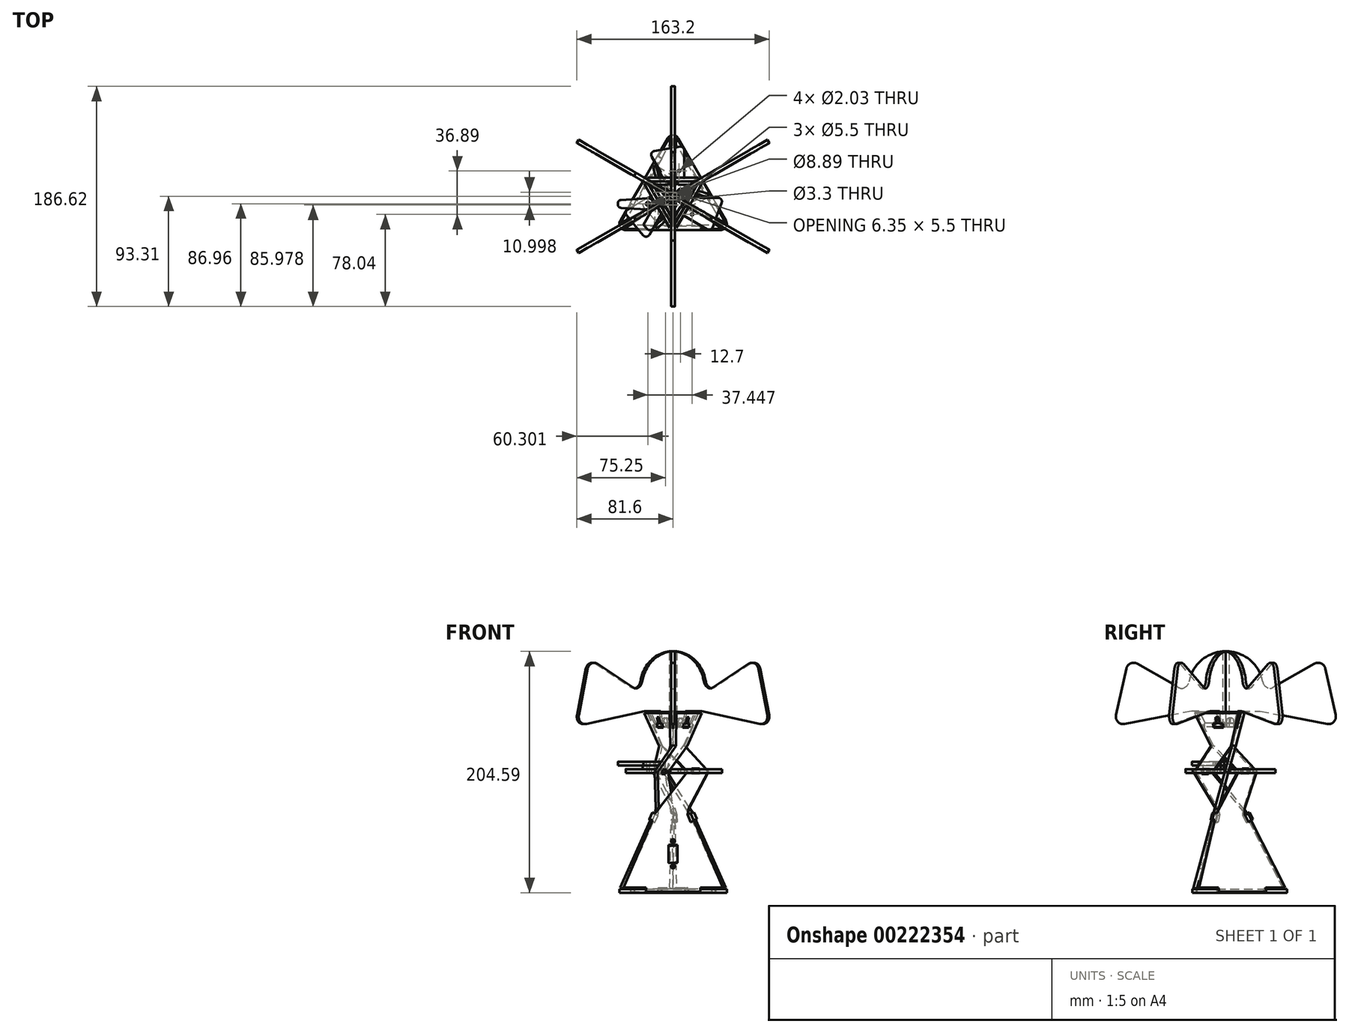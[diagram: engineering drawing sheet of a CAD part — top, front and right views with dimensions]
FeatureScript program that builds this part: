
annotation { "Feature Type Name" : "Feature", "Feature Type Description" : "" }
export const myFeature = defineFeature(function(context is Context, id is Id, definition is map)
    precondition{}
    {
        {
            var Q0;
            Q0=qCreatedBy(makeId("Front.planeOp"),FACE);
            var sketch = newSketch(context, id + "F0", { "sketchPlane" : qUnion([Q0])});
            skLineSegment(sketch, "E0", {"start": v(0, 0) * mm, "end": v(0, 152.4) * mm});
            skSolve(sketch);
        }
        {
            var Q0;
            Q0=qCreatedBy(makeId("Right.planeOp"),FACE);
            var sketch = newSketch(context, id + "F1", { "sketchPlane" : qUnion([Q0])});
            skLineSegment(sketch, "E1", {"start": v(0, 0) * mm, "end": v(-25.4, 0) * mm});
            skLineSegment(sketch, "E2", {"start": v(-25.4, 0) * mm, "end": v(15.88, 152.4) * mm});
            skLineSegment(sketch, "E3", {"start": v(15.88, 152.4) * mm, "end": v(0, 152.4) * mm});
            skLineSegment(sketch, "E4", {"start": v(0, 152.4) * mm, "end": v(0, 0) * mm});
            skPoint(sketch, "E5", {"position": v(0, 93.78) * mm});
            skSolve(sketch);
        }
        {
            var Q0;
            Q0=sQuery(id+"F1.wireOp",EDGE,"E2");
            var Q1;
            Q1=qCreatedBy(makeId("Front.planeOp"),FACE);
            cPlane(context, id + "F2", {"entities" : qUnion([Q0, Q1]), "cplaneType" : CPlaneType.LINE_ANGLE, "offset" : 25.4 * mm, "angle" : 0 * degree, "width" : 152.4 * mm, "height" : 152.4 * mm});
        }
        {
            var Q0;
            Q0=qCreatedBy(id+"F2.planeOp",FACE);
            var sketch = newSketch(context, id + "F3", { "sketchPlane" : qUnion([Q0])});
            skLineSegment(sketch, "E6", {"start": v(-43.56, -6.64) * mm, "end": v(43.56, -6.64) * mm});
            skLineSegment(sketch, "E7", {"start": v(43.56, -6.64) * mm, "end": v(15.2, 62.08) * mm});
            skLineSegment(sketch, "E8", {"start": v(15.2, 62.08) * mm, "end": v(-12.3, 99.06) * mm});
            skLineSegment(sketch, "E9", {"start": v(-12.3, 99.06) * mm, "end": v(9.57, 122.12) * mm});
            skLineSegment(sketch, "E10", {"start": v(9.57, 122.12) * mm, "end": v(21.59, 151.25) * mm});
            skLineSegment(sketch, "E11", {"start": v(21.59, 151.25) * mm, "end": v(-21.6, 151.25) * mm});
            skLineSegment(sketch, "E12", {"start": v(-21.6, 151.25) * mm, "end": v(-9.57, 122.12) * mm});
            skLineSegment(sketch, "E13", {"start": v(-9.57, 122.12) * mm, "end": v(-29.83, 99.06) * mm});
            skLineSegment(sketch, "E14", {"start": v(-29.83, 99.06) * mm, "end": v(-13.3, 66.7) * mm});
            skLineSegment(sketch, "E15", {"start": v(-13.3, 66.7) * mm, "end": v(-43.56, -6.64) * mm});
            skLineSegment(sketch, "E16", {"start": v(-42.1, -3.08) * mm, "end": v(-23.04, -3.08) * mm});
            skLineSegment(sketch, "E17", {"start": v(-23.04, -3.08) * mm, "end": v(-23.04, -6.64) * mm});
            skLineSegment(sketch, "E18", {"start": v(23.04, -6.64) * mm, "end": v(23.04, -3.08) * mm});
            skLineSegment(sketch, "E19", {"start": v(23.04, -3.08) * mm, "end": v(42.1, -3.08) * mm});
            skSolve(sketch);
        }
        {
            var Q0;
            {var subQ6=sQuery(id+"F3.wireOp",EDGE,"E8");Q0=makeQuery(id+"F3.imprint","IMPRINT",FACE,{"disambiguationData":[TD([[makeQuery(id+"F3.imprint","IMPRINT",EDGE,{"derivedFrom":subQ6}),1.0]])]});}
            extrude(context, id + "F4", {"entities" : qUnion([Q0]), "oppositeDirection" : true, "depth" : 3.17 * mm});
        }
        {
            var Q0;
            Q0=makeQuery(id+"F4.opExtrude","CAP_FACE",FACE,{"disambiguationData":[OSD([sQuery(id+"F3.wireOp",EDGE,"E6"),sQuery(id+"F3.wireOp",EDGE,"E7"),sQuery(id+"F3.wireOp",EDGE,"E8"),sQuery(id+"F3.wireOp",EDGE,"E9"),sQuery(id+"F3.wireOp",EDGE,"E10"),sQuery(id+"F3.wireOp",EDGE,"E11"),sQuery(id+"F3.wireOp",EDGE,"E12"),sQuery(id+"F3.wireOp",EDGE,"E13"),sQuery(id+"F3.wireOp",EDGE,"E14"),sQuery(id+"F3.wireOp",EDGE,"E15")])],"isStart":false});
            var sketch = newSketch(context, id + "F5", { "sketchPlane" : qUnion([Q0])});
            skLineSegment(sketch, "E20", {"start": v(-15.2, 62.08) * mm, "end": v(-17.55, 63.05) * mm});
            skLineSegment(sketch, "E21", {"start": v(-17.55, 63.05) * mm, "end": v(-19.97, 57.18) * mm});
            skLineSegment(sketch, "E22", {"start": v(-19.97, 57.18) * mm, "end": v(-17.63, 56.21) * mm});
            skLineSegment(sketch, "E23", {"start": v(-17.63, 56.21) * mm, "end": v(-15.2, 62.08) * mm});
            skSolve(sketch);
        }
        {
            var Q0;
            Q0 = qSketchRegion(id + "F5", true);
            extrude(context, id + "F6", {"entities" : qUnion([Q0]), "operationType" : NewBodyOperationType.ADD, "oppositeDirection" : true, "depth" : 3.17 * mm});
        }
        {
            var Q0;
            Q0=makeQuery(id+"F6.boolean.opBoolean","MERGE",FACE,{"derivedFrom":[makeQuery(id+"F4.opExtrude","CAP_FACE",FACE,{"disambiguationData":[OSD([sQuery(id+"F3.wireOp",EDGE,"E6"),sQuery(id+"F3.wireOp",EDGE,"E7"),sQuery(id+"F3.wireOp",EDGE,"E8"),sQuery(id+"F3.wireOp",EDGE,"E9"),sQuery(id+"F3.wireOp",EDGE,"E10"),sQuery(id+"F3.wireOp",EDGE,"E11"),sQuery(id+"F3.wireOp",EDGE,"E12"),sQuery(id+"F3.wireOp",EDGE,"E13"),sQuery(id+"F3.wireOp",EDGE,"E14"),sQuery(id+"F3.wireOp",EDGE,"E15")])],"isStart":false}),makeQuery(id+"F6.opExtrude","CAP_FACE",FACE,{"disambiguationData":[OSD([sQuery(id+"F5.wireOp",EDGE,"E20"),sQuery(id+"F5.wireOp",EDGE,"E21"),sQuery(id+"F5.wireOp",EDGE,"E22"),sQuery(id+"F5.wireOp",EDGE,"E23")])],"isStart":true})]});
            var sketch = newSketch(context, id + "F7", { "sketchPlane" : qUnion([Q0])});
            skLineSegment(sketch, "E24", {"start": v(12.2, 61.04) * mm, "end": v(14.82, 54.7) * mm});
            skLineSegment(sketch, "E25", {"start": v(12.2, 61.04) * mm, "end": v(15.14, 62.25) * mm});
            skLineSegment(sketch, "E26", {"start": v(17.75, 55.9) * mm, "end": v(15.14, 62.25) * mm});
            skLineSegment(sketch, "E27", {"start": v(17.75, 55.9) * mm, "end": v(14.82, 54.7) * mm});
            skLineSegment(sketch, "E28", {"start": v(13.3, 66.7) * mm, "end": v(12.2, 61.04) * mm});
            skLineSegment(sketch, "E29", {"start": v(15.14, 62.25) * mm, "end": v(13.3, 66.7) * mm});
            skSolve(sketch);
        }
        {
            var Q0;
            Q0 = qSketchRegion(id + "F7", true);
            extrude(context, id + "F8", {"entities" : qUnion([Q0]), "operationType" : NewBodyOperationType.REMOVE, "oppositeDirection" : true, "depth" : 25.4 * mm});
        }
        {
            var Q0;
            Q0=qCreatedBy(id+"F2.planeOp",FACE);
            var sketch = newSketch(context, id + "F9", { "sketchPlane" : qUnion([Q0])});
            skLineSegment(sketch, "E30.bottom", {"start": v(4.76, 142.08) * mm, "end": v(-4.76, 142.08) * mm});
            skLineSegment(sketch, "E30.top", {"start": v(4.76, 138.14) * mm, "end": v(-4.76, 138.14) * mm});
            skLineSegment(sketch, "E30.left", {"start": v(4.76, 142.08) * mm, "end": v(4.76, 138.14) * mm});
            skLineSegment(sketch, "E30.right", {"start": v(-4.76, 142.08) * mm, "end": v(-4.76, 138.14) * mm});
            skPoint(sketch, "E31", {"position": v(0, 138.14) * mm});
            skLineSegment(sketch, "E32.top", {"start": v(-1.59, 147.41) * mm, "end": v(1.59, 147.41) * mm});
            skLineSegment(sketch, "E32.left", {"start": v(-1.59, 142.08) * mm, "end": v(-1.59, 147.41) * mm});
            skLineSegment(sketch, "E32.right", {"start": v(1.59, 142.08) * mm, "end": v(1.59, 147.41) * mm});
            skLineSegment(sketch, "E33", {"start": v(0, 147.41) * mm, "end": v(0, 138.14) * mm, "construction": true});
            skSolve(sketch);
        }
        {
            var Q0;
            Q0 = qSketchRegion(id + "F9", true);
            extrude(context, id + "F10", {"entities" : qUnion([Q0]), "operationType" : NewBodyOperationType.REMOVE, "oppositeDirection" : true, "depth" : 25.4 * mm});
        }
        {
            var Q0;
            Q0=makeQuery(id+"F6.boolean.opBoolean","MERGE",FACE,{"derivedFrom":[makeQuery(id+"F4.opExtrude","CAP_FACE",FACE,{"disambiguationData":[OSD([sQuery(id+"F3.wireOp",EDGE,"E6"),sQuery(id+"F3.wireOp",EDGE,"E7"),sQuery(id+"F3.wireOp",EDGE,"E8"),sQuery(id+"F3.wireOp",EDGE,"E9"),sQuery(id+"F3.wireOp",EDGE,"E10"),sQuery(id+"F3.wireOp",EDGE,"E11"),sQuery(id+"F3.wireOp",EDGE,"E12"),sQuery(id+"F3.wireOp",EDGE,"E13"),sQuery(id+"F3.wireOp",EDGE,"E14"),sQuery(id+"F3.wireOp",EDGE,"E15"),sQuery(id+"F3.wireOp",EDGE,"E16"),sQuery(id+"F3.wireOp",EDGE,"E17"),sQuery(id+"F3.wireOp",EDGE,"E18"),sQuery(id+"F3.wireOp",EDGE,"E19")])],"isStart":false}),makeQuery(id+"F6.opExtrude","CAP_FACE",FACE,{"disambiguationData":[OSD([sQuery(id+"F5.wireOp",EDGE,"E20"),sQuery(id+"F5.wireOp",EDGE,"E21"),sQuery(id+"F5.wireOp",EDGE,"E22"),sQuery(id+"F5.wireOp",EDGE,"E23")])],"isStart":true})]});
            var sketch = newSketch(context, id + "F11", { "sketchPlane" : qUnion([Q0])});
            skLineSegment(sketch, "E34.bottom", {"start": v(15.88, 97.66) * mm, "end": v(22.48, 97.66) * mm});
            skLineSegment(sketch, "E34.top", {"start": v(15.88, 101.6) * mm, "end": v(22.48, 101.6) * mm});
            skLineSegment(sketch, "E34.left", {"start": v(15.88, 101.6) * mm, "end": v(15.88, 97.66) * mm});
            skLineSegment(sketch, "E34.right", {"start": v(22.48, 101.6) * mm, "end": v(22.48, 97.66) * mm});
            skSolve(sketch);
        }
        {
            var Q0;
            Q0 = qSketchRegion(id + "F11", true);
            extrude(context, id + "F12", {"entities" : qUnion([Q0]), "operationType" : NewBodyOperationType.REMOVE, "oppositeDirection" : true, "depth" : 25.4 * mm});
        }
        {
            var Q0;
            Q0=makeQuery(id+"F4.opExtrude","SWEPT_BODY",BODY,{"disambiguationData":[OSD([sQuery(id+"F3.wireOp",EDGE,"E6"),sQuery(id+"F3.wireOp",EDGE,"E7"),sQuery(id+"F3.wireOp",EDGE,"E8"),sQuery(id+"F3.wireOp",EDGE,"E9"),sQuery(id+"F3.wireOp",EDGE,"E10"),sQuery(id+"F3.wireOp",EDGE,"E11"),sQuery(id+"F3.wireOp",EDGE,"E12"),sQuery(id+"F3.wireOp",EDGE,"E13"),sQuery(id+"F3.wireOp",EDGE,"E14"),sQuery(id+"F3.wireOp",EDGE,"E15")])]});
            var Q1;
            Q1=sQuery(id+"F1.wireOp",EDGE,"E4");
            circularPattern(context, id + "F13", {"entities" : qUnion([Q0]), "axis" : qUnion([Q1]), "angle" : 360 * degree, "instanceCount" : 3, "equalSpace" : true});
        }
        {
            var Q0;
            Q0=makeQuery(id+"F10.boolean.opBoolean","INTERSECT",VERTEX,{"derivedFrom":[makeQuery(id+"F6.boolean.opBoolean","MERGE",FACE,{"derivedFrom":[makeQuery(id+"F4.opExtrude","CAP_FACE",FACE,{"disambiguationData":[OSD([sQuery(id+"F3.wireOp",EDGE,"E6"),sQuery(id+"F3.wireOp",EDGE,"E7"),sQuery(id+"F3.wireOp",EDGE,"E8"),sQuery(id+"F3.wireOp",EDGE,"E9"),sQuery(id+"F3.wireOp",EDGE,"E10"),sQuery(id+"F3.wireOp",EDGE,"E11"),sQuery(id+"F3.wireOp",EDGE,"E12"),sQuery(id+"F3.wireOp",EDGE,"E13"),sQuery(id+"F3.wireOp",EDGE,"E14"),sQuery(id+"F3.wireOp",EDGE,"E15")])],"isStart":false}),makeQuery(id+"F6.opExtrude","CAP_FACE",FACE,{"disambiguationData":[OSD([sQuery(id+"F5.wireOp",EDGE,"E20"),sQuery(id+"F5.wireOp",EDGE,"E21"),sQuery(id+"F5.wireOp",EDGE,"E22"),sQuery(id+"F5.wireOp",EDGE,"E23")])],"isStart":true})]}),makeQuery(id+"F10.opExtrude","SWEPT_FACE",FACE,{"disambiguationData":[OSD([sQuery(id+"F9.wireOp",EDGE,"E30.top")])]}),makeQuery(id+"F10.opExtrude","SWEPT_FACE",FACE,{"disambiguationData":[OSD([sQuery(id+"F9.wireOp",EDGE,"E30.right")])]})]});
            var Q1;
            Q1=makeQuery(id+"F13.opPattern","COPY",VERTEX,{"derivedFrom":makeQuery(id+"F10.boolean.opBoolean","INTERSECT",VERTEX,{"derivedFrom":[makeQuery(id+"F6.boolean.opBoolean","MERGE",FACE,{"derivedFrom":[makeQuery(id+"F4.opExtrude","CAP_FACE",FACE,{"disambiguationData":[OSD([sQuery(id+"F3.wireOp",EDGE,"E6"),sQuery(id+"F3.wireOp",EDGE,"E7"),sQuery(id+"F3.wireOp",EDGE,"E8"),sQuery(id+"F3.wireOp",EDGE,"E9"),sQuery(id+"F3.wireOp",EDGE,"E10"),sQuery(id+"F3.wireOp",EDGE,"E11"),sQuery(id+"F3.wireOp",EDGE,"E12"),sQuery(id+"F3.wireOp",EDGE,"E13"),sQuery(id+"F3.wireOp",EDGE,"E14"),sQuery(id+"F3.wireOp",EDGE,"E15")])],"isStart":false}),makeQuery(id+"F6.opExtrude","CAP_FACE",FACE,{"disambiguationData":[OSD([sQuery(id+"F5.wireOp",EDGE,"E20"),sQuery(id+"F5.wireOp",EDGE,"E21"),sQuery(id+"F5.wireOp",EDGE,"E22"),sQuery(id+"F5.wireOp",EDGE,"E23")])],"isStart":true})]}),makeQuery(id+"F10.opExtrude","SWEPT_FACE",FACE,{"disambiguationData":[OSD([sQuery(id+"F9.wireOp",EDGE,"E30.top")])]}),makeQuery(id+"F10.opExtrude","SWEPT_FACE",FACE,{"disambiguationData":[OSD([sQuery(id+"F9.wireOp",EDGE,"E30.right")])]})]}),"instanceName":"1"});
            var Q2;
            Q2=makeQuery(id+"F13.opPattern","COPY",VERTEX,{"derivedFrom":makeQuery(id+"F10.boolean.opBoolean","INTERSECT",VERTEX,{"derivedFrom":[makeQuery(id+"F6.boolean.opBoolean","MERGE",FACE,{"derivedFrom":[makeQuery(id+"F4.opExtrude","CAP_FACE",FACE,{"disambiguationData":[OSD([sQuery(id+"F3.wireOp",EDGE,"E6"),sQuery(id+"F3.wireOp",EDGE,"E7"),sQuery(id+"F3.wireOp",EDGE,"E8"),sQuery(id+"F3.wireOp",EDGE,"E9"),sQuery(id+"F3.wireOp",EDGE,"E10"),sQuery(id+"F3.wireOp",EDGE,"E11"),sQuery(id+"F3.wireOp",EDGE,"E12"),sQuery(id+"F3.wireOp",EDGE,"E13"),sQuery(id+"F3.wireOp",EDGE,"E14"),sQuery(id+"F3.wireOp",EDGE,"E15")])],"isStart":false}),makeQuery(id+"F6.opExtrude","CAP_FACE",FACE,{"disambiguationData":[OSD([sQuery(id+"F5.wireOp",EDGE,"E20"),sQuery(id+"F5.wireOp",EDGE,"E21"),sQuery(id+"F5.wireOp",EDGE,"E22"),sQuery(id+"F5.wireOp",EDGE,"E23")])],"isStart":true})]}),makeQuery(id+"F10.opExtrude","SWEPT_FACE",FACE,{"disambiguationData":[OSD([sQuery(id+"F9.wireOp",EDGE,"E30.top")])]}),makeQuery(id+"F10.opExtrude","SWEPT_FACE",FACE,{"disambiguationData":[OSD([sQuery(id+"F9.wireOp",EDGE,"E30.right")])]})]}),"instanceName":"2"});
            cPlane(context, id + "F14", {"entities" : qUnion([Q0, Q1, Q2]), "cplaneType" : CPlaneType.THREE_POINT, "offset" : 25.4 * mm, "width" : 152.4 * mm, "height" : 152.4 * mm});
        }
        {
            var Q0;
            Q0=qCreatedBy(id+"F14.planeOp",FACE);
            var sketch = newSketch(context, id + "F15", { "sketchPlane" : qUnion([Q0])});
            skLineSegment(sketch, "E35", {"start": v(-16.98, 9.8) * mm, "end": v(-10.71, -1.05) * mm});
            skLineSegment(sketch, "E36", {"start": v(-10.71, -1.05) * mm, "end": v(-13.35, -2.58) * mm});
            skLineSegment(sketch, "E37", {"start": v(-13.35, -2.58) * mm, "end": v(-8.9, -10.28) * mm});
            skLineSegment(sketch, "E38", {"start": v(-8.9, -10.28) * mm, "end": v(-6.27, -8.75) * mm});
            skLineSegment(sketch, "E39", {"start": v(-6.27, -8.75) * mm, "end": v(0, -19.6) * mm});
            skLineSegment(sketch, "E40", {"start": v(-11.13, -6.43) * mm, "end": v(-8.13, -4.7) * mm, "construction": true});
            skLineSegment(sketch, "E41.1.0", {"start": v(0, -19.6) * mm, "end": v(6.27, -8.75) * mm});
            skLineSegment(sketch, "E41.1.1", {"start": v(6.27, -8.75) * mm, "end": v(8.9, -10.28) * mm});
            skLineSegment(sketch, "E41.1.2", {"start": v(8.9, -10.28) * mm, "end": v(13.35, -2.58) * mm});
            skLineSegment(sketch, "E41.1.3", {"start": v(10.71, -1.05) * mm, "end": v(16.98, 9.8) * mm});
            skLineSegment(sketch, "E41.1.4", {"start": v(13.35, -2.58) * mm, "end": v(10.71, -1.05) * mm});
            skLineSegment(sketch, "E41.2.0", {"start": v(16.98, 9.8) * mm, "end": v(4.44, 9.8) * mm});
            skLineSegment(sketch, "E41.2.1", {"start": v(4.44, 9.8) * mm, "end": v(4.44, 12.85) * mm});
            skLineSegment(sketch, "E41.2.2", {"start": v(4.44, 12.85) * mm, "end": v(-4.45, 12.85) * mm});
            skLineSegment(sketch, "E41.2.3", {"start": v(-4.45, 9.8) * mm, "end": v(-16.98, 9.8) * mm});
            skLineSegment(sketch, "E41.2.4", {"start": v(-4.45, 12.85) * mm, "end": v(-4.45, 9.8) * mm});
            skPoint(sketch, "E41.center", {"position": v(0, 0) * mm});
            skCircle(sketch, "E42", {"center": v(6.35, 3.67) * mm, "radius": 2.75 * mm});
            skCircle(sketch, "E43", {"center": v(0, -7.33) * mm, "radius": 2.75 * mm});
            skCircle(sketch, "E44", {"center": v(-6.35, 3.67) * mm, "radius": 2.75 * mm});
            skLineSegment(sketch, "E45", {"start": v(-6.35, 3.67) * mm, "end": v(6.35, 3.67) * mm, "construction": true});
            skLineSegment(sketch, "E46", {"start": v(6.35, 3.67) * mm, "end": v(0, -7.33) * mm, "construction": true});
            skLineSegment(sketch, "E47", {"start": v(-6.35, 3.67) * mm, "end": v(0, -7.33) * mm, "construction": true});
            skLineSegment(sketch, "E48", {"start": v(0, -7.33) * mm, "end": v(0, 3.67) * mm, "construction": true});
            skLineSegment(sketch, "E49", {"start": v(-6.35, 3.67) * mm, "end": v(3.17, -1.83) * mm, "construction": true});
            skSolve(sketch);
        }
        {
            var Q0;
            Q0 = qSketchRegion(id + "F15", true);
            extrude(context, id + "F16", {"entities" : qUnion([Q0]), "depth" : 3.17 * mm});
        }
        {
            var Q0;
            Q0=qCreatedBy(makeId("Right.planeOp"),FACE);
            var sketch = newSketch(context, id + "F17", { "sketchPlane" : qUnion([Q0])});
            skLineSegment(sketch, "E50", {"start": v(-17.46, 143.75) * mm, "end": v(-22.6, 153.91) * mm});
            skLineSegment(sketch, "E51", {"start": v(-17.46, 143.75) * mm, "end": v(10.24, 143.75) * mm, "construction": true});
            skLineSegment(sketch, "E52", {"start": v(10.24, 143.75) * mm, "end": v(13, 153.91) * mm});
            skLineSegment(sketch, "E53", {"start": v(13, 153.91) * mm, "end": v(28.95, 153.91) * mm});
            skLineSegment(sketch, "E54", {"start": v(-22.6, 153.91) * mm, "end": v(-28.95, 153.91) * mm});
            skLineSegment(sketch, "E55", {"start": v(-4.58, 143.75) * mm, "end": v(-4.58, 145.34) * mm});
            skLineSegment(sketch, "E56", {"start": v(-4.58, 145.34) * mm, "end": v(-10.08, 145.34) * mm, "construction": true});
            skLineSegment(sketch, "E57", {"start": v(-10.08, 145.34) * mm, "end": v(-10.08, 143.75) * mm});
            skArc(sketch, "E58", {"start": v(-4.58, 145.34) * mm, "mid": v(-7.33, 148.09) * mm, "end": v(-10.08, 145.34) * mm});
            skLineSegment(sketch, "E59", {"start": v(10.24, 143.75) * mm, "end": v(-4.58, 143.75) * mm});
            skLineSegment(sketch, "E60", {"start": v(-10.08, 143.75) * mm, "end": v(-17.46, 143.75) * mm});
            skLineSegment(sketch, "E61", {"start": v(28.95, 153.91) * mm, "end": v(95.25, 141.21) * mm});
            skLineSegment(sketch, "E62", {"start": v(95.25, 141.21) * mm, "end": v(82.55, 198.36) * mm});
            skLineSegment(sketch, "E63", {"start": v(82.55, 198.36) * mm, "end": v(38.1, 172.96) * mm});
            skLineSegment(sketch, "E64", {"start": v(38.1, 172.96) * mm, "end": v(31.75, 172.96) * mm});
            skArc(sketch, "E65", {"start": v(31.75, 172.96) * mm, "mid": v(0, 204.71) * mm, "end": v(-31.75, 172.96) * mm});
            skLineSegment(sketch, "E66.MirrorCS", {"start": v(-38.1, 172.96) * mm, "end": v(-31.75, 172.96) * mm});
            skLineSegment(sketch, "E67.MirrorCS", {"start": v(-82.55, 198.36) * mm, "end": v(-38.1, 172.96) * mm});
            skLineSegment(sketch, "E68.MirrorCS", {"start": v(-28.95, 153.91) * mm, "end": v(-95.25, 141.21) * mm});
            skLineSegment(sketch, "E69.MirrorCS", {"start": v(-95.25, 141.21) * mm, "end": v(-82.55, 198.36) * mm});
            skLineSegment(sketch, "E70", {"start": v(10.24, 143.75) * mm, "end": v(12.87, 143.75) * mm});
            skLineSegment(sketch, "E71", {"start": v(12.87, 143.75) * mm, "end": v(14.2, 148.65) * mm});
            skLineSegment(sketch, "E72", {"start": v(14.2, 148.65) * mm, "end": v(11.75, 149.32) * mm});
            skSolve(sketch);
        }
        {
            var Q0;
            Q0 = qSketchRegion(id + "F17", true);
            extrude(context, id + "F18", {"entities" : qUnion([Q0]), "endBound" : BoundingType.SYMMETRIC, "depth" : 3.17 * mm});
        }
        {
            var Q0;
            Q0=makeQuery(id+"F18.opExtrude","SWEPT_EDGE",EDGE,{"disambiguationData":[OSD([sQuery(id+"F17.wireOp",EDGE,"E61"),sQuery(id+"F17.wireOp",EDGE,"E62")])]});
            var Q1;
            Q1=makeQuery(id+"F18.opExtrude","SWEPT_EDGE",EDGE,{"disambiguationData":[OSD([sQuery(id+"F17.wireOp",EDGE,"E62"),sQuery(id+"F17.wireOp",EDGE,"E63")])]});
            var Q2;
            Q2=makeQuery(id+"F18.opExtrude","SWEPT_EDGE",EDGE,{"disambiguationData":[OSD([sQuery(id+"F17.wireOp",EDGE,"E68.MirrorCS"),sQuery(id+"F17.wireOp",EDGE,"E69.MirrorCS")])]});
            var Q3;
            Q3=makeQuery(id+"F18.opExtrude","SWEPT_EDGE",EDGE,{"disambiguationData":[OSD([sQuery(id+"F17.wireOp",EDGE,"E67.MirrorCS"),sQuery(id+"F17.wireOp",EDGE,"E69.MirrorCS")])]});
            fillet(context, id + "F19", {"entities" : qUnion([Q0, Q1, Q2, Q3]), "radius" : 6.35 * mm, "tangentPropagation" : true, "allowEdgeOverflow" : false});
        }
        {
            var Q0;
            Q0=makeQuery(id+"F18.opExtrude","SWEPT_EDGE",EDGE,{"disambiguationData":[OSD([sQuery(id+"F17.wireOp",EDGE,"E63"),sQuery(id+"F17.wireOp",EDGE,"E64")])]});
            var Q1;
            Q1=makeQuery(id+"F18.opExtrude","SWEPT_EDGE",EDGE,{"disambiguationData":[OSD([sQuery(id+"F17.wireOp",EDGE,"E64"),sQuery(id+"F17.wireOp",EDGE,"E65")])]});
            var Q2;
            Q2=makeQuery(id+"F18.opExtrude","SWEPT_EDGE",EDGE,{"disambiguationData":[OSD([sQuery(id+"F17.wireOp",EDGE,"E65"),sQuery(id+"F17.wireOp",EDGE,"E66.MirrorCS")])]});
            var Q3;
            Q3=makeQuery(id+"F18.opExtrude","SWEPT_EDGE",EDGE,{"disambiguationData":[OSD([sQuery(id+"F17.wireOp",EDGE,"E66.MirrorCS"),sQuery(id+"F17.wireOp",EDGE,"E67.MirrorCS")])]});
            fillet(context, id + "F20", {"entities" : qUnion([Q0, Q1, Q2, Q3]), "radius" : 7.62 * mm, "tangentPropagation" : true, "allowEdgeOverflow" : false});
        }
        {
            var Q0;
            Q0=makeQuery(id+"F18.opExtrude","SWEPT_BODY",BODY,{"disambiguationData":[OSD([sQuery(id+"F17.wireOp",EDGE,"E50"),sQuery(id+"F17.wireOp",EDGE,"E52"),sQuery(id+"F17.wireOp",EDGE,"E53"),sQuery(id+"F17.wireOp",EDGE,"E54"),sQuery(id+"F17.wireOp",EDGE,"E55"),sQuery(id+"F17.wireOp",EDGE,"E57"),sQuery(id+"F17.wireOp",EDGE,"E58"),sQuery(id+"F17.wireOp",EDGE,"E59"),sQuery(id+"F17.wireOp",EDGE,"E60"),sQuery(id+"F17.wireOp",EDGE,"E61"),sQuery(id+"F17.wireOp",EDGE,"E62"),sQuery(id+"F17.wireOp",EDGE,"E63"),sQuery(id+"F17.wireOp",EDGE,"E64"),sQuery(id+"F17.wireOp",EDGE,"E65"),sQuery(id+"F17.wireOp",EDGE,"E66.MirrorCS"),sQuery(id+"F17.wireOp",EDGE,"E67.MirrorCS"),sQuery(id+"F17.wireOp",EDGE,"E68.MirrorCS"),sQuery(id+"F17.wireOp",EDGE,"E69.MirrorCS")])]});
            var Q1;
            Q1=sQuery(id+"F0.wireOp",EDGE,"E0");
            circularPattern(context, id + "F21", {"entities" : qUnion([Q0]), "axis" : qUnion([Q1]), "angle" : 360 * degree, "instanceCount" : 3, "equalSpace" : true});
        }
        {
            var Q0;
            Q0=qCreatedBy(id+"F14.planeOp",FACE);
            var sketch = newSketch(context, id + "F22", { "sketchPlane" : qUnion([Q0])});
            skCircle(sketch, "E73.cCircle", {"center": v(0, 0) * mm, "radius": 2.75 * mm, "construction": true});
            skLineSegment(sketch, "E73.0", {"start": v(-1.59, 2.75) * mm, "end": v(1.59, 2.75) * mm});
            skLineSegment(sketch, "E73.1", {"start": v(1.59, 2.75) * mm, "end": v(3.18, 0) * mm});
            skLineSegment(sketch, "E73.2", {"start": v(3.17, 0) * mm, "end": v(1.59, -2.75) * mm});
            skLineSegment(sketch, "E73.3", {"start": v(1.59, -2.75) * mm, "end": v(-1.59, -2.75) * mm});
            skLineSegment(sketch, "E73.4", {"start": v(-1.59, -2.75) * mm, "end": v(-3.18, 0) * mm});
            skLineSegment(sketch, "E73.5", {"start": v(-3.17, 0) * mm, "end": v(-1.59, 2.75) * mm});
            skPoint(sketch, "E73.0.midPoint", {"position": v(0, 2.75) * mm});
            skPoint(sketch, "E74", {"position": v(1.59, 2.75) * mm});
            skSolve(sketch);
        }
        {
            var Q0;
            Q0 = qSketchRegion(id + "F22", true);
            extrude(context, id + "F23", {"entities" : qUnion([Q0]), "operationType" : NewBodyOperationType.REMOVE, "depth" : 19.05 * mm});
        }
        {
            var Q0;
            Q0 = qSketchRegion(id + "F22", true);
            extrude(context, id + "F24", {"entities" : qUnion([Q0]), "operationType" : NewBodyOperationType.REMOVE, "endBound" : BoundingType.THROUGH_ALL, "depth" : 38.1 * mm, "hasSecondDirection" : true, "secondDirectionOppositeDirection" : false, "secondDirectionDepth" : 19.05 * mm});
        }
        {
            var Q0;
            Q0 = qSketchRegion(id + "F22", true);
            extrude(context, id + "F25", {"entities" : qUnion([Q0]), "operationType" : NewBodyOperationType.REMOVE, "endBound" : BoundingType.THROUGH_ALL, "depth" : 25.4 * mm, "hasSecondDirection" : true, "secondDirectionOppositeDirection" : false, "secondDirectionDepth" : 38.1 * mm});
        }
        {
            var Q0;
            Q0=qCreatedBy(makeId("Top.planeOp"),FACE);
            cPlane(context, id + "F26", {"entities" : qUnion([Q0]), "cplaneType" : CPlaneType.OFFSET, "offset" : 101.6 * mm, "width" : 152.4 * mm, "height" : 152.4 * mm});
        }
        {
            var Q0;
            Q0=qCreatedBy(id+"F26.planeOp",FACE);
            cPlane(context, id + "F27", {"entities" : qUnion([Q0]), "cplaneType" : CPlaneType.OFFSET, "offset" : 3.17 * mm, "width" : 152.4 * mm, "height" : 152.4 * mm});
        }
        {
            var Q0;
            Q0=qCreatedBy(id+"F27.planeOp",FACE);
            var sketch = newSketch(context, id + "F28", { "sketchPlane" : qUnion([Q0])});
            skPoint(sketch, "E75", {"position": v(-2.22, -9.8) * mm});
            skSolve(sketch);
        }
        {
            var Q0;
            Q0=qCreatedBy(id+"F26.planeOp",FACE);
            var sketch = newSketch(context, id + "F29", { "sketchPlane" : qUnion([Q0])});
            skLineSegment(sketch, "E76", {"start": v(29.16, -1.17) * mm, "end": v(11.33, -1.17) * mm});
            skPoint(sketch, "E77.0", {"position": v(-2.22, -9.8) * mm});
            skLineSegment(sketch, "E78", {"start": v(-2.22, -9.8) * mm, "end": v(32.25, -29.7) * mm});
            skLineSegment(sketch, "E79", {"start": v(32.25, -29.7) * mm, "end": v(42.84, -1.17) * mm});
            skLineSegment(sketch, "E80", {"start": v(42.84, -1.17) * mm, "end": v(29.16, -1.17) * mm});
            skLineSegment(sketch, "E81.1.0", {"start": v(9.6, 2.98) * mm, "end": v(9.6, 42.78) * mm});
            skLineSegment(sketch, "E81.1.1", {"start": v(9.6, 42.78) * mm, "end": v(-20.4, 37.7) * mm});
            skLineSegment(sketch, "E81.1.2", {"start": v(-20.4, 37.7) * mm, "end": v(-13.57, 25.84) * mm});
            skLineSegment(sketch, "E81.1.3", {"start": v(-13.57, 25.84) * mm, "end": v(-4.65, 10.4) * mm});
            skLineSegment(sketch, "E81.2.0", {"start": v(-7.38, 6.82) * mm, "end": v(-41.85, -13.08) * mm});
            skLineSegment(sketch, "E81.2.1", {"start": v(-41.85, -13.08) * mm, "end": v(-22.44, -36.52) * mm});
            skLineSegment(sketch, "E81.2.2", {"start": v(-22.44, -36.52) * mm, "end": v(-15.6, -24.67) * mm});
            skLineSegment(sketch, "E81.2.3", {"start": v(-15.6, -24.67) * mm, "end": v(-6.68, -9.22) * mm});
            skPoint(sketch, "E81.center", {"position": v(0, 0) * mm});
            skLineSegment(sketch, "E82", {"start": v(-6.68, -9.22) * mm, "end": v(-2.22, -9.8) * mm});
            skLineSegment(sketch, "E83", {"start": v(-7.38, 6.82) * mm, "end": v(-4.65, 10.4) * mm});
            skLineSegment(sketch, "E84", {"start": v(9.6, 2.98) * mm, "end": v(11.33, -1.17) * mm});
            skCircle(sketch, "E85", {"center": v(0, 0) * mm, "radius": 4.45 * mm});
            skCircle(sketch, "E86", {"center": v(-21.3, -6.35) * mm, "radius": 1.02 * mm});
            skCircle(sketch, "E87.1.0", {"center": v(16.15, -15.27) * mm, "radius": 1.02 * mm});
            skCircle(sketch, "E87.2.0", {"center": v(5.15, 21.62) * mm, "radius": 1.02 * mm});
            skLineSegment(sketch, "E88", {"start": v(-9.02, -13.27) * mm, "end": v(-6.38, -14.8) * mm});
            skLineSegment(sketch, "E89", {"start": v(-6.38, -14.8) * mm, "end": v(-9.55, -20.3) * mm});
            skLineSegment(sketch, "E90", {"start": v(-9.55, -20.3) * mm, "end": v(-12.2, -18.77) * mm});
            skLineSegment(sketch, "E91.1.0", {"start": v(22.35, 1.88) * mm, "end": v(22.35, -1.17) * mm});
            skLineSegment(sketch, "E91.1.1", {"start": v(16, 1.88) * mm, "end": v(22.35, 1.88) * mm});
            skLineSegment(sketch, "E91.1.2", {"start": v(16, -1.17) * mm, "end": v(16, 1.88) * mm});
            skLineSegment(sketch, "E91.2.0", {"start": v(-12.8, 18.42) * mm, "end": v(-10.16, 19.94) * mm});
            skLineSegment(sketch, "E91.2.1", {"start": v(-9.63, 12.92) * mm, "end": v(-12.8, 18.42) * mm});
            skLineSegment(sketch, "E91.2.2", {"start": v(-6.99, 14.44) * mm, "end": v(-9.63, 12.92) * mm});
            skSolve(sketch);
        }
        {
            var Q0;
            Q0 = qSketchRegion(id + "F29", true);
            extrude(context, id + "F30", {"entities" : qUnion([Q0]), "depth" : 3.17 * mm});
        }
        {
            var Q0;
            Q0=makeQuery(id+"F30.opExtrude","SWEPT_EDGE",EDGE,{"disambiguationData":[OSD([sQuery(id+"F29.wireOp",EDGE,"E81.1.1"),sQuery(id+"F29.wireOp",EDGE,"E81.1.2")])]});
            var Q1;
            Q1=makeQuery(id+"F30.opExtrude","SWEPT_EDGE",EDGE,{"disambiguationData":[OSD([sQuery(id+"F29.wireOp",EDGE,"E81.1.0"),sQuery(id+"F29.wireOp",EDGE,"E81.1.1")])]});
            var Q2;
            Q2=makeQuery(id+"F30.opExtrude","SWEPT_EDGE",EDGE,{"disambiguationData":[OSD([sQuery(id+"F29.wireOp",EDGE,"E81.2.0"),sQuery(id+"F29.wireOp",EDGE,"E81.2.1")])]});
            var Q3;
            Q3=makeQuery(id+"F30.opExtrude","SWEPT_EDGE",EDGE,{"disambiguationData":[OSD([sQuery(id+"F29.wireOp",EDGE,"E81.2.1"),sQuery(id+"F29.wireOp",EDGE,"E81.2.2")])]});
            var Q4;
            Q4=makeQuery(id+"F30.opExtrude","SWEPT_EDGE",EDGE,{"disambiguationData":[OSD([sQuery(id+"F29.wireOp",EDGE,"E78"),sQuery(id+"F29.wireOp",EDGE,"E79")])]});
            var Q5;
            Q5=makeQuery(id+"F30.opExtrude","SWEPT_EDGE",EDGE,{"disambiguationData":[OSD([sQuery(id+"F29.wireOp",EDGE,"E79"),sQuery(id+"F29.wireOp",EDGE,"E80")])]});
            fillet(context, id + "F31", {"entities" : qUnion([Q0, Q1, Q2, Q3, Q4, Q5]), "radius" : 3.17 * mm, "tangentPropagation" : true, "allowEdgeOverflow" : false});
        }
        {
            var Q0;
            Q0=qCreatedBy(makeId("Top.planeOp"),FACE);
            var sketch = newSketch(context, id + "F32", { "sketchPlane" : qUnion([Q0])});
            skLineSegment(sketch, "E92", {"start": v(32.71, -7.72) * mm, "end": v(9.67, 32.2) * mm});
            skLineSegment(sketch, "E93", {"start": v(9.67, 32.2) * mm, "end": v(13.13, 34.19) * mm});
            skLineSegment(sketch, "E94", {"start": v(13.13, 34.19) * mm, "end": v(0, 56.93) * mm});
            skLineSegment(sketch, "E95", {"start": v(32.71, -7.72) * mm, "end": v(36.17, -5.72) * mm});
            skLineSegment(sketch, "E96", {"start": v(36.17, -5.72) * mm, "end": v(49.3, -28.46) * mm});
            skLineSegment(sketch, "E97.1.0", {"start": v(-13.13, 34.19) * mm, "end": v(0, 56.93) * mm});
            skLineSegment(sketch, "E97.1.1", {"start": v(-9.67, 32.2) * mm, "end": v(-13.13, 34.19) * mm});
            skLineSegment(sketch, "E97.1.2", {"start": v(-9.67, 32.2) * mm, "end": v(-32.71, -7.72) * mm});
            skLineSegment(sketch, "E97.1.3", {"start": v(-32.71, -7.72) * mm, "end": v(-36.17, -5.72) * mm});
            skLineSegment(sketch, "E97.1.4", {"start": v(-36.17, -5.72) * mm, "end": v(-49.3, -28.46) * mm});
            skLineSegment(sketch, "E97.2.0", {"start": v(-23.04, -28.46) * mm, "end": v(-49.3, -28.46) * mm});
            skLineSegment(sketch, "E97.2.1", {"start": v(-23.04, -24.47) * mm, "end": v(-23.04, -28.46) * mm});
            skLineSegment(sketch, "E97.2.2", {"start": v(-23.04, -24.47) * mm, "end": v(23.04, -24.47) * mm});
            skLineSegment(sketch, "E97.2.3", {"start": v(23.04, -24.47) * mm, "end": v(23.04, -28.46) * mm});
            skLineSegment(sketch, "E97.2.4", {"start": v(23.04, -28.46) * mm, "end": v(49.3, -28.46) * mm});
            skPoint(sketch, "E97.center", {"position": v(0, 0) * mm});
            skSolve(sketch);
        }
        {
            var Q0;
            Q0 = qSketchRegion(id + "F32", true);
            extrude(context, id + "F33", {"entities" : qUnion([Q0]), "depth" : 3.17 * mm});
        }
        {
            var Q0;
            Q0=makeQuery(id+"F33.opExtrude","SWEPT_EDGE",EDGE,{"disambiguationData":[OSD([sQuery(id+"F32.wireOp",EDGE,"E94"),sQuery(id+"F32.wireOp",EDGE,"E97.1.0")])]});
            var Q1;
            Q1=makeQuery(id+"F33.opExtrude","SWEPT_EDGE",EDGE,{"disambiguationData":[OSD([sQuery(id+"F32.wireOp",EDGE,"E97.1.4"),sQuery(id+"F32.wireOp",EDGE,"E97.2.0")])]});
            var Q2;
            Q2=makeQuery(id+"F33.opExtrude","SWEPT_EDGE",EDGE,{"disambiguationData":[OSD([sQuery(id+"F32.wireOp",EDGE,"E96"),sQuery(id+"F32.wireOp",EDGE,"E97.2.4")])]});
            fillet(context, id + "F34", {"entities" : qUnion([Q0, Q1, Q2]), "radius" : 5.08 * mm, "tangentPropagation" : true, "allowEdgeOverflow" : false});
        }
        {
            var Q0;
            Q0=makeQuery(id+"F16.opExtrude","SWEPT_EDGE",EDGE,{"disambiguationData":[OSD([sQuery(id+"F15.wireOp",EDGE,"E35"),sQuery(id+"F15.wireOp",EDGE,"E41.2.3")])]});
            var Q1;
            Q1=makeQuery(id+"F16.opExtrude","SWEPT_EDGE",EDGE,{"disambiguationData":[OSD([sQuery(id+"F15.wireOp",EDGE,"E41.1.3"),sQuery(id+"F15.wireOp",EDGE,"E41.2.0")])]});
            var Q2;
            Q2=makeQuery(id+"F16.opExtrude","SWEPT_EDGE",EDGE,{"disambiguationData":[OSD([sQuery(id+"F15.wireOp",EDGE,"E39"),sQuery(id+"F15.wireOp",EDGE,"E41.1.0")])]});
            fillet(context, id + "F35", {"entities" : qUnion([Q0, Q1, Q2]), "radius" : 1.27 * mm, "tangentPropagation" : true, "allowEdgeOverflow" : false});
        }
        {
            var Q0;
            Q0=makeQuery(id+"F30.opExtrude","CAP_FACE",FACE,{"disambiguationData":[OSD([sQuery(id+"F29.wireOp",EDGE,"E76"),sQuery(id+"F29.wireOp",EDGE,"E78"),sQuery(id+"F29.wireOp",EDGE,"E79"),sQuery(id+"F29.wireOp",EDGE,"E80"),sQuery(id+"F29.wireOp",EDGE,"E81.1.0"),sQuery(id+"F29.wireOp",EDGE,"E81.1.1"),sQuery(id+"F29.wireOp",EDGE,"E81.1.2"),sQuery(id+"F29.wireOp",EDGE,"E81.1.3"),sQuery(id+"F29.wireOp",EDGE,"E81.2.0"),sQuery(id+"F29.wireOp",EDGE,"E81.2.1"),sQuery(id+"F29.wireOp",EDGE,"E81.2.2"),sQuery(id+"F29.wireOp",EDGE,"E81.2.3"),sQuery(id+"F29.wireOp",EDGE,"E82"),sQuery(id+"F29.wireOp",EDGE,"E83"),sQuery(id+"F29.wireOp",EDGE,"E84"),sQuery(id+"F29.wireOp",EDGE,"E85"),sQuery(id+"F29.wireOp",EDGE,"E86"),sQuery(id+"F29.wireOp",EDGE,"E87.1.0"),sQuery(id+"F29.wireOp",EDGE,"E87.2.0"),sQuery(id+"F29.wireOp",EDGE,"E88"),sQuery(id+"F29.wireOp",EDGE,"E89"),sQuery(id+"F29.wireOp",EDGE,"E90"),sQuery(id+"F29.wireOp",EDGE,"E91.1.0"),sQuery(id+"F29.wireOp",EDGE,"E91.1.1"),sQuery(id+"F29.wireOp",EDGE,"E91.1.2"),sQuery(id+"F29.wireOp",EDGE,"E91.2.0"),sQuery(id+"F29.wireOp",EDGE,"E91.2.1"),sQuery(id+"F29.wireOp",EDGE,"E91.2.2")])],"isStart":false});
            var sketch = newSketch(context, id + "F36", { "sketchPlane" : qUnion([Q0])});
            skLineSegment(sketch, "E98", {"start": v(-17.87, -3.51) * mm, "end": v(-15.1, -6.86) * mm});
            skLineSegment(sketch, "E99", {"start": v(-15.1, -6.86) * mm, "end": v(-10.73, -4.33) * mm});
            skLineSegment(sketch, "E100", {"start": v(-10.73, -4.33) * mm, "end": v(-6.68, -9.22) * mm});
            skLineSegment(sketch, "E101", {"start": v(-6.68, -9.22) * mm, "end": v(-14.08, -22.04) * mm});
            skLineSegment(sketch, "E102", {"start": v(-14.08, -22.04) * mm, "end": v(-22.14, -12.3) * mm});
            skLineSegment(sketch, "E103", {"start": v(-22.14, -12.3) * mm, "end": v(-24.73, -9.19) * mm});
            skArc(sketch, "E104", {"start": v(-17.87, -3.51) * mm, "mid": v(-24.14, -2.92) * mm, "end": v(-24.73, -9.19) * mm});
            skCircle(sketch, "E105.0", {"center": v(-21.3, -6.35) * mm, "radius": 1.02 * mm});
            skSolve(sketch);
        }
        {
            var Q0;
            Q0 = qSketchRegion(id + "F36", true);
            extrude(context, id + "F37", {"entities" : qUnion([Q0]), "depth" : 3.17 * mm});
        }
        {
            var Q0;
            Q0=makeQuery(id+"F37.opExtrude","SWEPT_EDGE",EDGE,{"disambiguationData":[OSD([sQuery(id+"F29.wireOp",EDGE,"E81.2.2"),sQuery(id+"F29.wireOp",EDGE,"E81.2.3"),sQuery(id+"F36.wireOp",EDGE,"E101"),sQuery(id+"F36.wireOp",EDGE,"E102")])]});
            fillet(context, id + "F38", {"entities" : qUnion([Q0]), "radius" : 3.17 * mm, "tangentPropagation" : true, "allowEdgeOverflow" : false});
        }
        {
            var Q0;
            Q0=makeQuery(id+"F37.opExtrude","CAP_FACE",FACE,{"disambiguationData":[OSD([sQuery(id+"F36.wireOp",EDGE,"E98"),sQuery(id+"F36.wireOp",EDGE,"E99"),sQuery(id+"F36.wireOp",EDGE,"E100"),sQuery(id+"F36.wireOp",EDGE,"E101"),sQuery(id+"F36.wireOp",EDGE,"E102"),sQuery(id+"F36.wireOp",EDGE,"E103"),sQuery(id+"F36.wireOp",EDGE,"E104"),sQuery(id+"F36.wireOp",EDGE,"E105.0")])],"isStart":false});
            var sketch = newSketch(context, id + "F39", { "sketchPlane" : qUnion([Q0])});
            skLineSegment(sketch, "E106.0", {"start": v(-10.73, -4.33) * mm, "end": v(-6.68, -9.22) * mm});
            skLineSegment(sketch, "E106.1", {"start": v(-15.1, -6.86) * mm, "end": v(-10.73, -4.33) * mm});
            skLineSegment(sketch, "E106.2", {"start": v(-6.68, -9.22) * mm, "end": v(-11.8, -18.09) * mm});
            skLineSegment(sketch, "E107", {"start": v(-15.1, -6.86) * mm, "end": v(-25, -23.98) * mm});
            skLineSegment(sketch, "E108", {"start": v(-25, -23.98) * mm, "end": v(-19.22, -30.95) * mm});
            skLineSegment(sketch, "E109", {"start": v(-19.22, -30.95) * mm, "end": v(-11.8, -18.09) * mm});
            skSolve(sketch);
        }
        {
            var Q0;
            Q0 = qSketchRegion(id + "F39", true);
            extrude(context, id + "F40", {"entities" : qUnion([Q0]), "depth" : 3.17 * mm});
        }
        {
            var Q0;
            Q0=makeQuery(id+"F40.opExtrude","SWEPT_EDGE",EDGE,{"disambiguationData":[OSD([sQuery(id+"F39.wireOp",EDGE,"E108"),sQuery(id+"F39.wireOp",EDGE,"E109")])]});
            fillet(context, id + "F41", {"entities" : qUnion([Q0]), "radius" : 3.17 * mm, "tangentPropagation" : true, "allowEdgeOverflow" : false});
        }
        {
            var Q0;
            Q0=makeQuery(id+"F37.opExtrude","CAP_FACE",FACE,{"disambiguationData":[OSD([sQuery(id+"F36.wireOp",EDGE,"E98"),sQuery(id+"F36.wireOp",EDGE,"E99"),sQuery(id+"F36.wireOp",EDGE,"E100"),sQuery(id+"F36.wireOp",EDGE,"E101"),sQuery(id+"F36.wireOp",EDGE,"E102"),sQuery(id+"F36.wireOp",EDGE,"E103"),sQuery(id+"F36.wireOp",EDGE,"E104"),sQuery(id+"F36.wireOp",EDGE,"E105.0")])],"isStart":false});
            var sketch = newSketch(context, id + "F42", { "sketchPlane" : qUnion([Q0])});
            skLineSegment(sketch, "E110", {"start": v(-21.6, -1.6) * mm, "end": v(-46.7, -3.18) * mm});
            skLineSegment(sketch, "E111", {"start": v(-46.7, -3.18) * mm, "end": v(-46.7, -9.52) * mm});
            skLineSegment(sketch, "E112", {"start": v(-46.7, -9.52) * mm, "end": v(-21.6, -11.1) * mm});
            skArc(sketch, "E113", {"start": v(-21.6, -11.1) * mm, "mid": v(-16.54, -6.35) * mm, "end": v(-21.6, -1.6) * mm});
            skCircle(sketch, "E114", {"center": v(-21.3, -6.35) * mm, "radius": 1.65 * mm});
            skLineSegment(sketch, "E115", {"start": v(-46.7, -6.35) * mm, "end": v(-21.3, -6.35) * mm, "construction": true});
            skSolve(sketch);
        }
        {
            var Q0;
            Q0 = qSketchRegion(id + "F42", true);
            extrude(context, id + "F43", {"entities" : qUnion([Q0]), "depth" : 3.17 * mm});
        }
        {
            var Q0;
            Q0=makeQuery(id+"F6.boolean.opBoolean","MERGE",FACE,{"derivedFrom":[makeQuery(id+"F4.opExtrude","CAP_FACE",FACE,{"disambiguationData":[OSD([sQuery(id+"F3.wireOp",EDGE,"E6"),sQuery(id+"F3.wireOp",EDGE,"E7"),sQuery(id+"F3.wireOp",EDGE,"E8"),sQuery(id+"F3.wireOp",EDGE,"E9"),sQuery(id+"F3.wireOp",EDGE,"E10"),sQuery(id+"F3.wireOp",EDGE,"E11"),sQuery(id+"F3.wireOp",EDGE,"E12"),sQuery(id+"F3.wireOp",EDGE,"E13"),sQuery(id+"F3.wireOp",EDGE,"E14"),sQuery(id+"F3.wireOp",EDGE,"E15"),sQuery(id+"F3.wireOp",EDGE,"E16"),sQuery(id+"F3.wireOp",EDGE,"E17"),sQuery(id+"F3.wireOp",EDGE,"E18"),sQuery(id+"F3.wireOp",EDGE,"E19")])],"isStart":false}),makeQuery(id+"F6.opExtrude","CAP_FACE",FACE,{"disambiguationData":[OSD([sQuery(id+"F5.wireOp",EDGE,"E20"),sQuery(id+"F5.wireOp",EDGE,"E21"),sQuery(id+"F5.wireOp",EDGE,"E22"),sQuery(id+"F5.wireOp",EDGE,"E23")])],"isStart":true})]});
            var sketch = newSketch(context, id + "F44", { "sketchPlane" : qUnion([Q0])});
            skLineSegment(sketch, "E116.bottom", {"start": v(-3.81, 34.64) * mm, "end": v(3.81, 34.64) * mm});
            skLineSegment(sketch, "E116.top", {"start": v(-3.81, 18.76) * mm, "end": v(3.81, 18.76) * mm});
            skLineSegment(sketch, "E116.left", {"start": v(-3.81, 34.64) * mm, "end": v(-3.8, 18.76) * mm});
            skLineSegment(sketch, "E116.right", {"start": v(3.8, 34.64) * mm, "end": v(3.8, 18.76) * mm});
            skPoint(sketch, "E117", {"position": v(0, 18.76) * mm});
            skCircle(sketch, "E118", {"center": v(0, 37.81) * mm, "radius": 1.63 * mm});
            skCircle(sketch, "E119", {"center": v(0, 15.59) * mm, "radius": 1.63 * mm});
            skLineSegment(sketch, "E120", {"start": v(-3.81, 26.7) * mm, "end": v(-11.97, 26.7) * mm, "construction": true});
            skSolve(sketch);
        }
        {
            var Q0;
            Q0 = qSketchRegion(id + "F44", true);
            extrude(context, id + "F45", {"entities" : qUnion([Q0]), "operationType" : NewBodyOperationType.REMOVE, "oppositeDirection" : true, "depth" : 25.4 * mm});
        }
        {
            var Q0;
            Q0=makeQuery(id+"F43.opExtrude","SWEPT_EDGE",EDGE,{"disambiguationData":[OSD([sQuery(id+"F42.wireOp",EDGE,"E111"),sQuery(id+"F42.wireOp",EDGE,"E112")])]});
            var Q1;
            Q1=makeQuery(id+"F43.opExtrude","SWEPT_EDGE",EDGE,{"disambiguationData":[OSD([sQuery(id+"F42.wireOp",EDGE,"E110"),sQuery(id+"F42.wireOp",EDGE,"E111")])]});
            fillet(context, id + "F46", {"entities" : qUnion([Q0, Q1]), "radius" : 2.54 * mm, "tangentPropagation" : true, "allowEdgeOverflow" : false});
        }
    });
